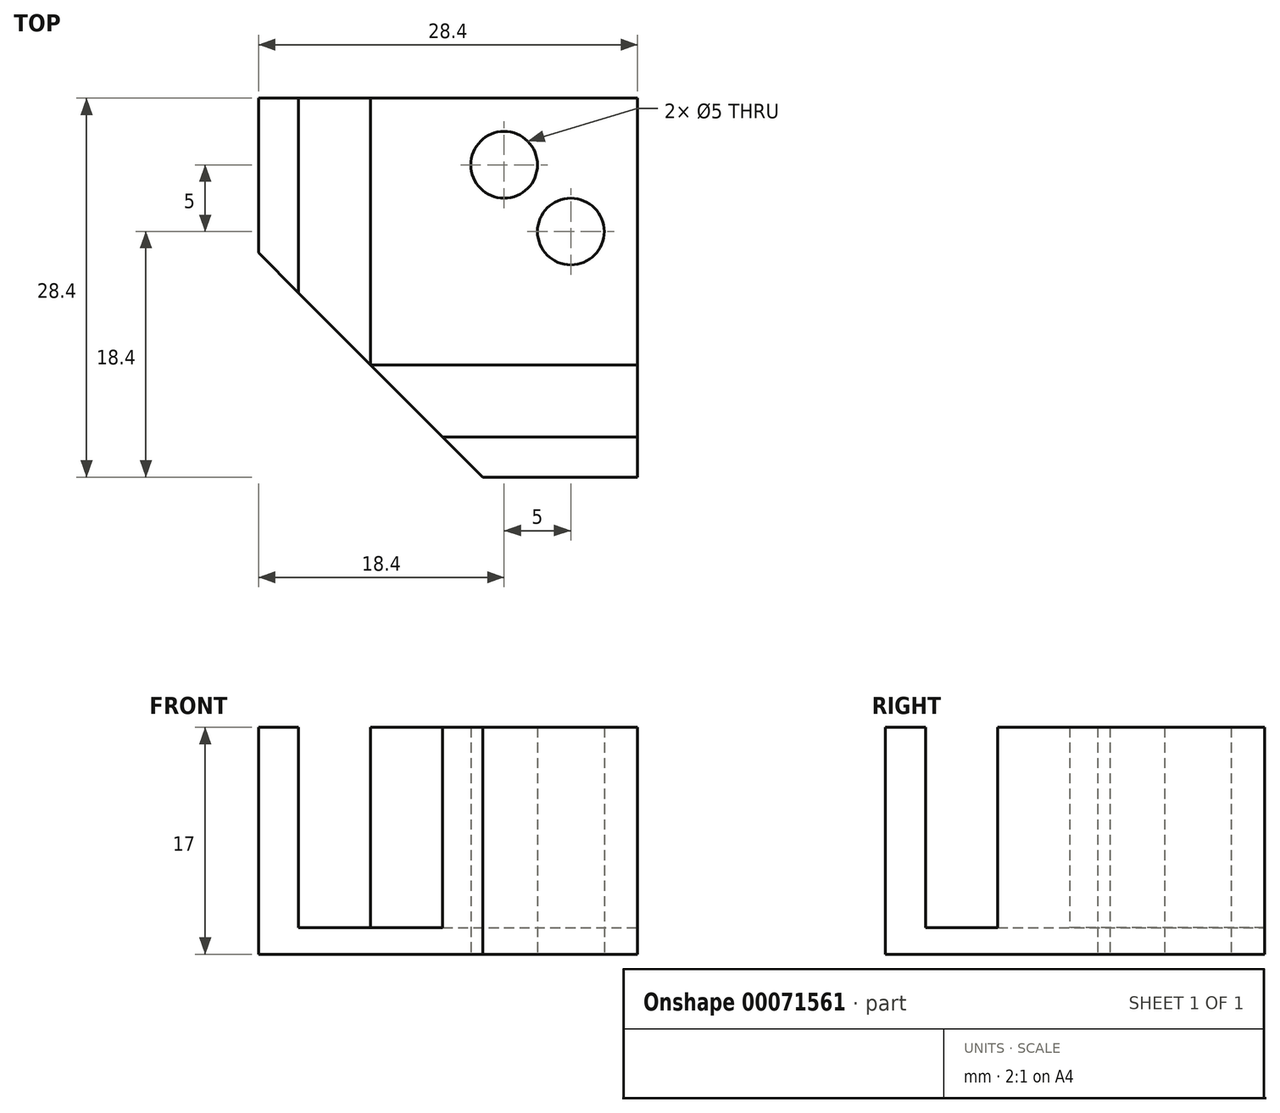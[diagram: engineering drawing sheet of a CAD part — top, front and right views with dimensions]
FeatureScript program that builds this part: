
annotation { "Feature Type Name" : "Feature", "Feature Type Description" : "" }
export const myFeature = defineFeature(function(context is Context, id is Id, definition is map)
    precondition{}
    {
        {
            var Q0;
            Q0=qCreatedBy(makeId("Top.planeOp"),FACE);
            var sketch = newSketch(context, id + "F0", { "sketchPlane" : qUnion([Q0])});
            skLineSegment(sketch, "E0.bottom", {"start": v(0, 0) * mm, "end": v(20, 0) * mm});
            skLineSegment(sketch, "E0.top", {"start": v(0, 20) * mm, "end": v(20, 20) * mm});
            skLineSegment(sketch, "E0.left", {"start": v(0, 0) * mm, "end": v(0, 20) * mm});
            skLineSegment(sketch, "E0.right", {"start": v(20, 0) * mm, "end": v(20, 20) * mm});
            skCircle(sketch, "E1", {"center": v(10, 15) * mm, "radius": 2.5 * mm});
            skCircle(sketch, "E2", {"center": v(15, 10) * mm, "radius": 2.5 * mm});
            skSolve(sketch);
        }
        {
            var Q0;
            Q0 = qSketchRegion(id + "F0", true);
            extrude(context, id + "F1", {"entities" : qUnion([Q0]), "depth" : 15 * mm});
        }
        {
            var Q0;
            Q0=qCreatedBy(makeId("Top.planeOp"),FACE);
            var sketch = newSketch(context, id + "F2", { "sketchPlane" : qUnion([Q0])});
            skLineSegment(sketch, "E3.bottom", {"start": v(-5.4, 20) * mm, "end": v(-8.4, 20) * mm});
            skLineSegment(sketch, "E3.top", {"start": v(-5.4, 8.4) * mm, "end": v(-8.4, 8.4) * mm, "construction": true});
            skLineSegment(sketch, "E3.left", {"start": v(-8.4, 20) * mm, "end": v(-8.4, 8.4) * mm});
            skLineSegment(sketch, "E3.right", {"start": v(-5.4, 20) * mm, "end": v(-5.4, 8.4) * mm});
            skLineSegment(sketch, "E4.bottom", {"start": v(20, -5.4) * mm, "end": v(8.4, -5.4) * mm});
            skLineSegment(sketch, "E4.top", {"start": v(20, -8.4) * mm, "end": v(8.4, -8.4) * mm});
            skLineSegment(sketch, "E4.left", {"start": v(20, -5.4) * mm, "end": v(20, -8.4) * mm});
            skLineSegment(sketch, "E4.right", {"start": v(8.4, -5.4) * mm, "end": v(8.4, -8.4) * mm, "construction": true});
            skLineSegment(sketch, "E5", {"start": v(-8.4, 8.4) * mm, "end": v(8.4, -8.4) * mm, "construction": true});
            skLineSegment(sketch, "E6", {"start": v(-5.4, 8.4) * mm, "end": v(-5.4, 5.4) * mm});
            skLineSegment(sketch, "E7", {"start": v(-5.4, 5.4) * mm, "end": v(-8.4, 8.4) * mm});
            skLineSegment(sketch, "E8", {"start": v(8.4, -5.4) * mm, "end": v(5.4, -5.4) * mm});
            skLineSegment(sketch, "E9", {"start": v(5.4, -5.4) * mm, "end": v(8.4, -8.4) * mm});
            skSolve(sketch);
        }
        {
            var Q0;
            Q0 = qSketchRegion(id + "F2", true);
            var Q1;
            Q1=makeQuery(id+"F1.opExtrude","CAP_FACE",FACE,{"disambiguationData":[OSD([sQuery(id+"F0.wireOp",EDGE,"E0.bottom"),sQuery(id+"F0.wireOp",EDGE,"E0.top"),sQuery(id+"F0.wireOp",EDGE,"E0.left"),sQuery(id+"F0.wireOp",EDGE,"E0.right"),sQuery(id+"F0.wireOp",EDGE,"E1")])],"isStart":false});
            extrude(context, id + "F3", {"entities" : qUnion([Q0]), "endBound" : BoundingType.UP_TO_SURFACE, "endBoundEntityFace" : qUnion([Q1]), "depth" : 25 * mm});
        }
        {
            var Q0;
            Q0=makeQuery(id+"F1.opExtrude","CAP_FACE",FACE,{"disambiguationData":[OSD([sQuery(id+"F0.wireOp",EDGE,"E0.bottom"),sQuery(id+"F0.wireOp",EDGE,"E0.top"),sQuery(id+"F0.wireOp",EDGE,"E0.left"),sQuery(id+"F0.wireOp",EDGE,"E0.right"),sQuery(id+"F0.wireOp",EDGE,"E1")])],"isStart":true});
            var sketch = newSketch(context, id + "F4", { "sketchPlane" : qUnion([Q0])});
            skLineSegment(sketch, "E10", {"start": v(20, -20) * mm, "end": v(20, 8.4) * mm});
            skLineSegment(sketch, "E11", {"start": v(20, 8.4) * mm, "end": v(8.4, 8.4) * mm});
            skLineSegment(sketch, "E12", {"start": v(8.4, 8.4) * mm, "end": v(-8.4, -8.4) * mm});
            skLineSegment(sketch, "E13", {"start": v(-8.4, -8.4) * mm, "end": v(-8.4, -20) * mm});
            skLineSegment(sketch, "E14", {"start": v(-8.4, -20) * mm, "end": v(20, -20) * mm});
            skCircle(sketch, "E15.0", {"center": v(10, -15) * mm, "radius": 2.5 * mm});
            skCircle(sketch, "E16.0", {"center": v(15, -10) * mm, "radius": 2.5 * mm});
            skSolve(sketch);
        }
        {
            var Q0;
            Q0 = qSketchRegion(id + "F4", true);
            extrude(context, id + "F5", {"entities" : qUnion([Q0]), "operationType" : NewBodyOperationType.ADD, "depth" : 2 * mm});
        }
    });
